# Revit family: gapped-FP-Revit20-en-EB60_BuiltInCoffeeMaker-incl-76cmTrimKits-0-9000xxxxA-NZ-AU
name_source: partatom
category: Specialty Equipment
units: mm (PartAtom-declared; Revit-internal decimal feet)

## family parameters
Always vertical = Yes
Cut with Voids When Loaded = Yes
OmniClass Number = 23.40.40.14.17.31
OmniClass Title = Small Specialized Cooking Equipment
Part Type = Normal
Room Calculation Point = No
Round Connector Dimension = Use Diameter
Shared = No
Work Plane-Based = No

## types (7) — shared parameters
Cavity - Depth = 550 mm
Cavity - Height = 450 mm
Cavity - Width = 560 mm  [stored 1.83727 ft]
Connector Description - Electrical = 220-240 V, 50 Hz, 10 A Service
Description = 30in Built-In Coffee Maker
Manufacturer = Fisher & Paykel Appliances
Opening - Height = 460 mm  [stored 1.50919 ft]
URL = www.fisherpaykel.com
Visibility - 2 x 1mm thick spacers = Yes
Visibility - Clearance Required = Yes
zero-valued in all types: Default Elevation

## per-type parameters (varying)
| type | Gap Lower - Height | Material - Front | Model | Opening - Depth | Opening - Width | Style - Front | Style - Trims | Type Comments | Visibility - Trim Kit |
| EB60MSG3 | 9 mm  [stored 0.0295276 ft] | Fisher & Paykel - Glass, Grey | EB60MSG3 | 20 mm  [stored 0.0656168 ft] | 600 mm  [stored 1.9685 ft] | 30in-76cm Coffee Fronts : Coffee Front Minimal (Grey) | 30in-76cm Coffee Trims : Coffee Trim Minimal (Grey) | Minimal Grey | No |
| EB76PSX3 | 13 mm | Fisher & Paykel - Stainless Steel | EB76PSX3 | 24 mm  [stored 0.0787402 ft] | 762 mm  [stored 2.5 ft] | 30in-76cm Coffee Fronts : Coffee Front Professional | 30in-76cm Coffee Trims : Coffee Trim Professional | Professional | Yes |
| EB60MSB3 | 9 mm  [stored 0.0295276 ft] | Fisher & Paykel - Glass, Black | EB60MSB4 | 20 mm  [stored 0.0656168 ft] | 600 mm  [stored 1.9685 ft] | 30in-76cm Coffee Fronts : Coffee Front Minimal (Black) | 30in-76cm Coffee Trims : Coffee Trim Minimal (Black) | Minimal Black | No |
| EB60CSX3 | 9 mm  [stored 0.0295276 ft] | Fisher & Paykel - Glass, Brushed | EB60CSX3 | 20 mm  [stored 0.0656168 ft] | 600 mm  [stored 1.9685 ft] | 30in-76cm Coffee Fronts : Coffee Front Contemporary | 30in-76cm Coffee Trims : Coffee Trim Contemporary | Contemporary | No |
| EB60CSX3 with TK7630NCX3 Trim Kit | 9 mm  [stored 0.0295276 ft] | Fisher & Paykel - Glass, Brushed | EB30CSX3 with TK7630NCX3 Trim Kit | 20 mm  [stored 0.0656168 ft] | 762 mm  [stored 2.5 ft] | 30in-76cm Coffee Fronts : Coffee Front Contemporary | 30in-76cm Coffee Trims : Coffee Trim Contemporary | Contemporary | Yes |
| EB60MSB3 with TK7630NMB3 Trim Kit | 9 mm  [stored 0.0295276 ft] | Fisher & Paykel - Glass, Black | EB60MSB3 with TK7630NMB3 Trim Kit | 20 mm  [stored 0.0656168 ft] | 762 mm  [stored 2.5 ft] | 30in-76cm Coffee Fronts : Coffee Front Minimal (Black) | 30in-76cm Coffee Trims : Coffee Trim Minimal (Black) | Minimal Black | No |
| EB60MSG3 with TK7630NMG3 Trim Kit | 9 mm  [stored 0.0295276 ft] | Fisher & Paykel - Glass, Grey | EB60MSG3 with TK7630NMG3 Trim Kit | 20 mm  [stored 0.0656168 ft] | 762 mm  [stored 2.5 ft] | 30in-76cm Coffee Fronts : Coffee Front Minimal (Grey) | 30in-76cm Coffee Trims : Coffee Trim Minimal (Grey) | Minimal Grey | Yes |

note: [stored X ft] marks values corroborated as IEEE doubles in the binary element streams (Revit-internal decimal feet)

## geometry (parser evidence)
native form markers: Sweep x9
no freeform markers — native parametric forms only
